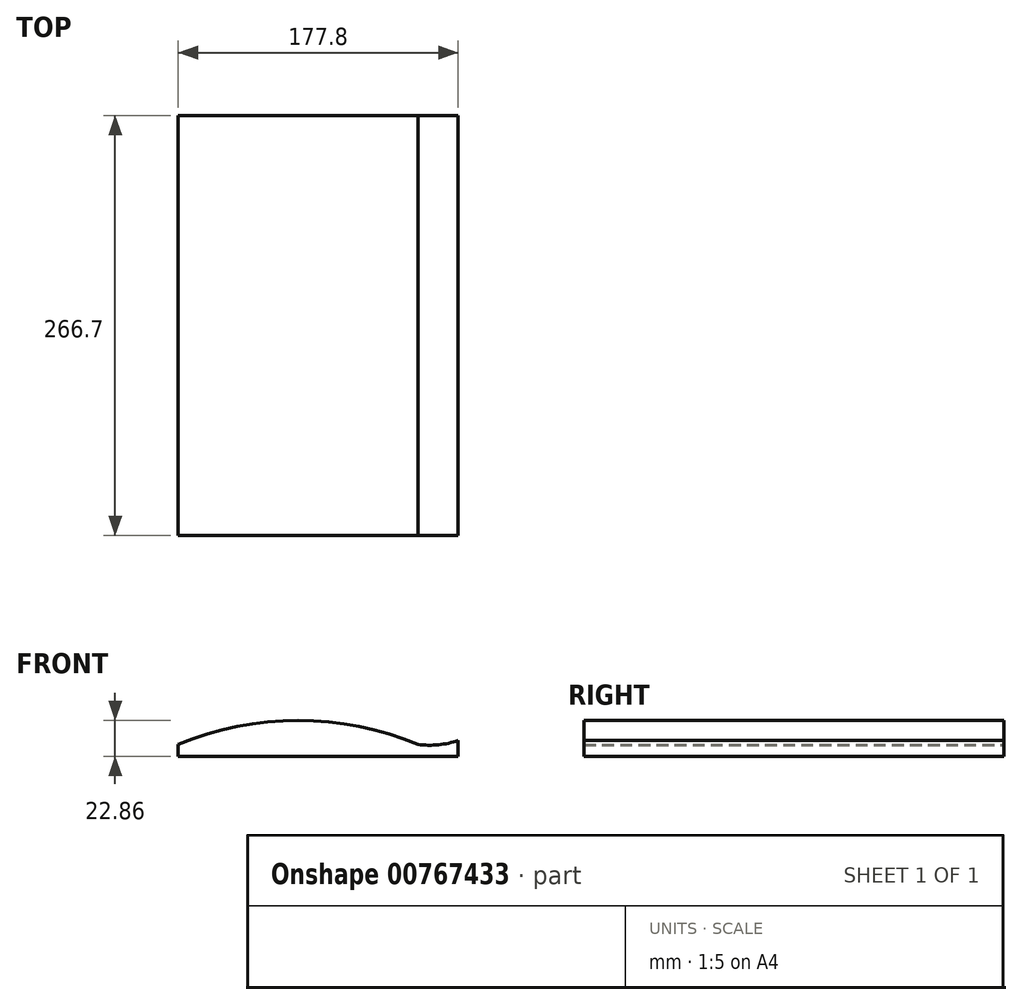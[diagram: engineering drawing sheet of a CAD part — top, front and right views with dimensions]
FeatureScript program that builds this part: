
annotation { "Feature Type Name" : "Feature", "Feature Type Description" : "" }
export const myFeature = defineFeature(function(context is Context, id is Id, definition is map)
    precondition{}
    {
        {
            var Q0;
            Q0=qCreatedBy(makeId("Front.planeOp"),FACE);
            var sketch = newSketch(context, id + "F0", { "sketchPlane" : qUnion([Q0])});
            skArc(sketch, "E0", {"start": v(22.86, 7.62) * mm, "mid": v(-53.34, 22.86) * mm, "end": v(-129.54, 7.62) * mm});
            skArc(sketch, "E1", {"start": v(22.86, 7.62) * mm, "mid": v(35.71, 7.36) * mm, "end": v(48.26, 10.16) * mm});
            skLineSegment(sketch, "E2", {"start": v(-129.54, 7.62) * mm, "end": v(-129.54, 0) * mm});
            skLineSegment(sketch, "E3", {"start": v(-129.54, 0) * mm, "end": v(48.26, 0) * mm});
            skLineSegment(sketch, "E4", {"start": v(48.26, 0) * mm, "end": v(48.26, 10.16) * mm});
            skLineSegment(sketch, "E5", {"start": v(0, 15.54) * mm, "end": v(0, 0) * mm});
            skSolve(sketch);
        }
        {
            var Q0;
            Q0=makeQuery(id+"F0.imprint","IMPRINT",FACE,{"disambiguationData":[TD([[makeQuery(id+"F0.imprint","IMPRINT",EDGE,{"derivedFrom":sQuery(id+"F0.wireOp",EDGE,"E0")}),1.0]])]});
            extrude(context, id + "F1", {"entities" : qUnion([Q0]), "depth" : 266.7 * mm, "offsetDistance" : 25.4 * mm});
        }
        {
            var Q0;
            Q0=makeQuery(id+"F0.imprint","IMPRINT",FACE,{"disambiguationData":[TD([[makeQuery(id+"F0.imprint","IMPRINT",EDGE,{"derivedFrom":sQuery(id+"F0.wireOp",EDGE,"E0")}),1.0]])]});
            var Q1;
            {var subQ1=sQuery(id+"F0.wireOp",EDGE,"E1");Q1=makeQuery(id+"F0.imprint","IMPRINT",FACE,{"disambiguationData":[TD([[makeQuery(id+"F0.imprint","IMPRINT",EDGE,{"derivedFrom":subQ1}),-1.0]])]});}
            extrude(context, id + "F2", {"entities" : qUnion([Q0, Q1]), "operationType" : NewBodyOperationType.ADD, "depth" : 266.7 * mm, "offsetDistance" : 25.4 * mm});
        }
    });
